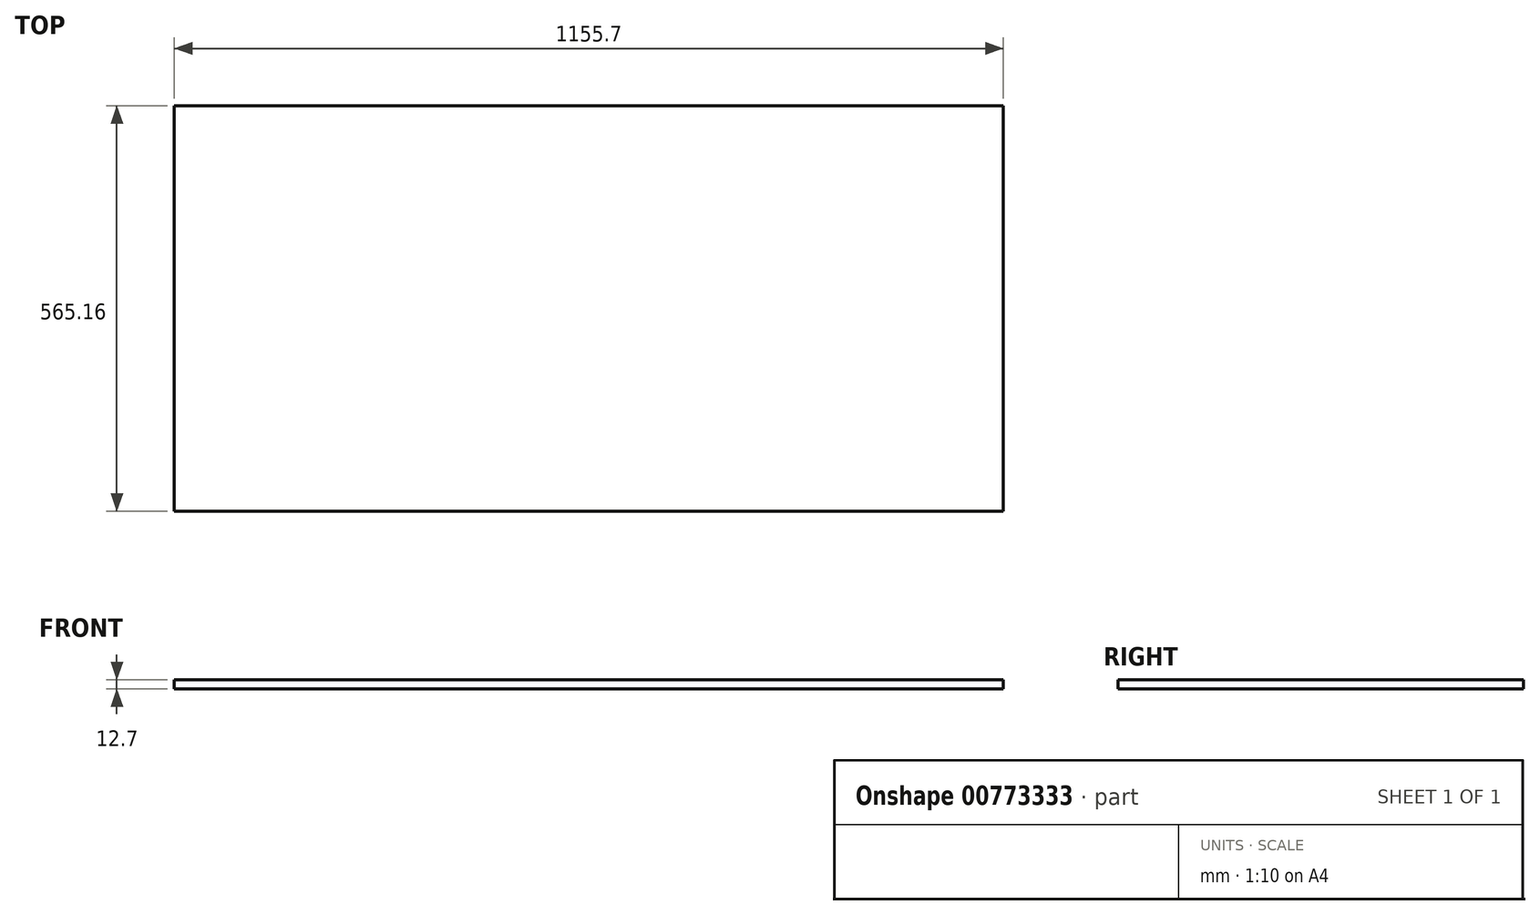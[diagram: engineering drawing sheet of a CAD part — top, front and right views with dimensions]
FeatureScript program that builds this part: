
annotation { "Feature Type Name" : "Feature", "Feature Type Description" : "" }
export const myFeature = defineFeature(function(context is Context, id is Id, definition is map)
    precondition{}
    {
        {
            var Q0;
            Q0=qCreatedBy(makeId("Top.planeOp"),FACE);
            var sketch = newSketch(context, id + "F0", { "sketchPlane" : qUnion([Q0])});
            skLineSegment(sketch, "E0.bottom", {"start": v(577.85, 282.58) * mm, "end": v(-577.85, 282.58) * mm});
            skLineSegment(sketch, "E0.top", {"start": v(577.85, -282.58) * mm, "end": v(-577.85, -282.58) * mm});
            skLineSegment(sketch, "E0.left", {"start": v(577.85, 282.58) * mm, "end": v(577.85, -282.58) * mm});
            skLineSegment(sketch, "E0.right", {"start": v(-577.85, 282.58) * mm, "end": v(-577.85, -282.58) * mm});
            skPoint(sketch, "E0.middle", {"position": v(0, 0) * mm});
            skSolve(sketch);
        }
        {
            var Q0;
            Q0=makeQuery(id+"F0.imprint","IMPRINT",FACE,{"disambiguationData":[TD([[makeQuery(id+"F0.imprint","IMPRINT",EDGE,{"derivedFrom":sQuery(id+"F0.wireOp",EDGE,"E0.bottom")}),1.0]])]});
            extrude(context, id + "F1", {"entities" : qUnion([Q0]), "depth" : 12.7 * mm, "offsetDistance" : 25.4 * mm});
        }
    });
